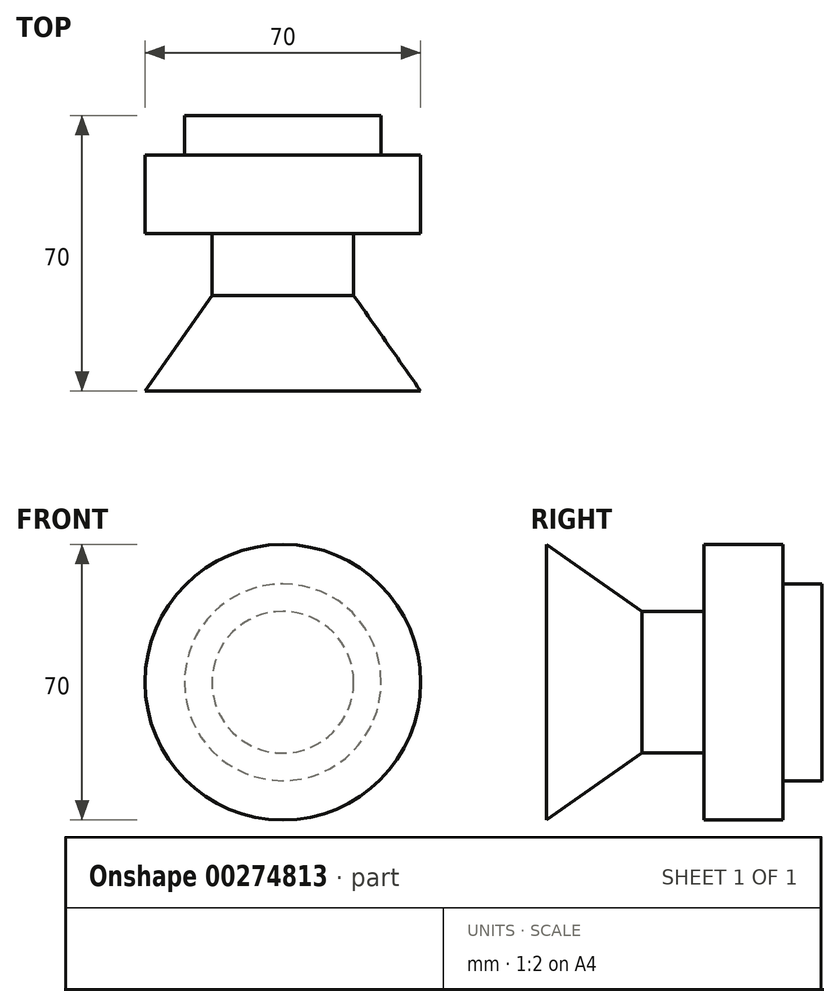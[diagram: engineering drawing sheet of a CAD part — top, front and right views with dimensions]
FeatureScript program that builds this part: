
annotation { "Feature Type Name" : "Feature", "Feature Type Description" : "" }
export const myFeature = defineFeature(function(context is Context, id is Id, definition is map)
    precondition{}
    {
        {
            var Q0;
            Q0=qCreatedBy(makeId("Top.planeOp"),FACE);
            var sketch = newSketch(context, id + "F0", { "sketchPlane" : qUnion([Q0])});
            skLineSegment(sketch, "E0", {"start": v(14.63, -21.34) * mm, "end": v(-20.37, -21.34) * mm});
            skLineSegment(sketch, "E1", {"start": v(-20.37, -21.34) * mm, "end": v(-3.37, 2.94) * mm});
            skLineSegment(sketch, "E2", {"start": v(-3.37, 2.94) * mm, "end": v(-3.37, 18.66) * mm});
            skLineSegment(sketch, "E3", {"start": v(-3.37, 18.66) * mm, "end": v(-20.37, 18.66) * mm});
            skLineSegment(sketch, "E4", {"start": v(-20.37, 18.66) * mm, "end": v(-20.37, 38.66) * mm});
            skLineSegment(sketch, "E5", {"start": v(-20.37, 38.66) * mm, "end": v(-10.37, 38.66) * mm});
            skLineSegment(sketch, "E6", {"start": v(-10.37, 38.66) * mm, "end": v(-10.37, 48.66) * mm});
            skLineSegment(sketch, "E7", {"start": v(-10.37, 48.66) * mm, "end": v(14.63, 48.66) * mm});
            skLineSegment(sketch, "E8", {"start": v(14.63, 48.66) * mm, "end": v(14.63, -21.34) * mm});
            skSolve(sketch);
        }
        {
            var Q0;
            Q0=makeQuery(id+"F0.imprint","IMPRINT",FACE,{"disambiguationData":[TD([[makeQuery(id+"F0.imprint","IMPRINT",EDGE,{"derivedFrom":sQuery(id+"F0.wireOp",EDGE,"E0")}),-1.0]])]});
            var Q1;
            Q1=sQuery(id+"F0.wireOp",EDGE,"E8");
            revolve(context, id + "F1", {"entities" : qUnion([Q0]), "axis" : qUnion([Q1]), "revolveType" : RevolveType.ONE_DIRECTION, "oppositeDirection" : true, "angle" : 360 * degree});
        }
    });
